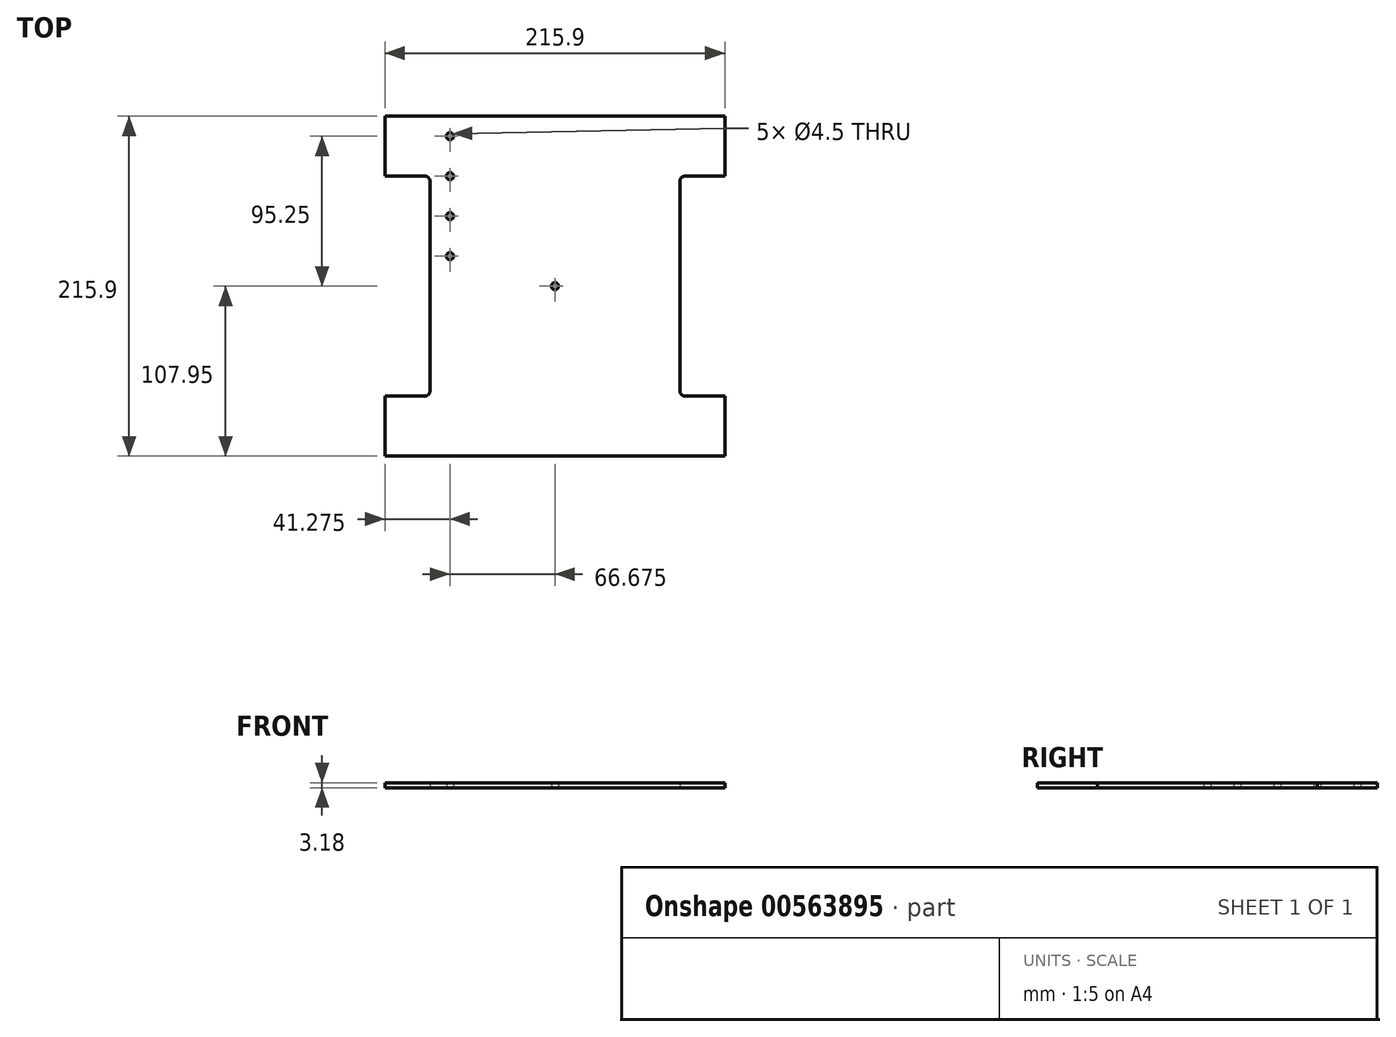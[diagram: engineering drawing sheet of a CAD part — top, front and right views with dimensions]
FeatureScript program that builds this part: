
annotation { "Feature Type Name" : "Feature", "Feature Type Description" : "" }
export const myFeature = defineFeature(function(context is Context, id is Id, definition is map)
    precondition{}
    {
        {
            var Q0;
            Q0=qCreatedBy(makeId("Top.planeOp"),FACE);
            var sketch = newSketch(context, id + "F0", { "sketchPlane" : qUnion([Q0])});
            skLineSegment(sketch, "E0", {"start": v(-107.95, -107.95) * mm, "end": v(107.95, -107.95) * mm});
            skLineSegment(sketch, "E1", {"start": v(107.95, -107.95) * mm, "end": v(107.95, -69.85) * mm});
            skLineSegment(sketch, "E2", {"start": v(107.95, -69.85) * mm, "end": v(82.55, -69.85) * mm});
            skLineSegment(sketch, "E3", {"start": v(79.37, -66.67) * mm, "end": v(79.37, 66.68) * mm});
            skLineSegment(sketch, "E4", {"start": v(82.55, 69.85) * mm, "end": v(107.95, 69.85) * mm});
            skLineSegment(sketch, "E5", {"start": v(107.95, 69.85) * mm, "end": v(107.95, 107.95) * mm});
            skLineSegment(sketch, "E6", {"start": v(107.95, 107.95) * mm, "end": v(-107.95, 107.95) * mm});
            skLineSegment(sketch, "E7", {"start": v(-107.95, 107.95) * mm, "end": v(-107.95, 69.85) * mm});
            skLineSegment(sketch, "E8", {"start": v(-107.95, 69.85) * mm, "end": v(-82.55, 69.85) * mm});
            skLineSegment(sketch, "E9", {"start": v(-79.38, 66.68) * mm, "end": v(-79.37, -66.68) * mm});
            skLineSegment(sketch, "E10", {"start": v(-82.55, -69.85) * mm, "end": v(-107.95, -69.85) * mm});
            skLineSegment(sketch, "E11", {"start": v(-107.95, -69.85) * mm, "end": v(-107.95, -107.95) * mm});
            skPoint(sketch, "E12.visualSharp", {"position": v(-79.38, 69.85) * mm});
            skArc(sketch, "E12.filletArc", {"start": v(-79.38, 66.68) * mm, "mid": v(-80.3, 68.92) * mm, "end": v(-82.55, 69.85) * mm});
            skPoint(sketch, "E13.visualSharp", {"position": v(79.37, 69.85) * mm});
            skArc(sketch, "E13.filletArc", {"start": v(82.55, 69.85) * mm, "mid": v(80.3, 68.92) * mm, "end": v(79.37, 66.68) * mm});
            skPoint(sketch, "E14.visualSharp", {"position": v(-79.37, -69.85) * mm});
            skArc(sketch, "E14.filletArc", {"start": v(-82.55, -69.85) * mm, "mid": v(-80.3, -68.92) * mm, "end": v(-79.37, -66.68) * mm});
            skPoint(sketch, "E15.visualSharp", {"position": v(79.37, -69.85) * mm});
            skArc(sketch, "E15.filletArc", {"start": v(79.37, -66.67) * mm, "mid": v(80.3, -68.92) * mm, "end": v(82.55, -69.85) * mm});
            skPoint(sketch, "E16", {"position": v(0, 0) * mm});
            skPoint(sketch, "E17", {"position": v(-69.85, 0) * mm});
            skPoint(sketch, "E18", {"position": v(-66.68, 95.25) * mm});
            skPoint(sketch, "E19", {"position": v(-66.68, 69.85) * mm});
            skPoint(sketch, "E20", {"position": v(-66.68, 44.45) * mm});
            skPoint(sketch, "E21", {"position": v(-66.68, 19.05) * mm});
            skPoint(sketch, "E22", {"position": v(65.86, 104.4) * mm});
            skPoint(sketch, "E23", {"position": v(65.86, 87.5) * mm});
            skPoint(sketch, "E24", {"position": v(65.86, 60.93) * mm});
            skPoint(sketch, "E25", {"position": v(65.86, 36.3) * mm});
            skPoint(sketch, "E26", {"position": v(65.86, 0) * mm});
            skPoint(sketch, "E27", {"position": v(65.86, -19.25) * mm});
            skPoint(sketch, "E28", {"position": v(65.86, -38.1) * mm});
            skPoint(sketch, "E29", {"position": v(65.86, -50.65) * mm});
            skPoint(sketch, "E30", {"position": v(65.86, -67.08) * mm});
            skPoint(sketch, "E31", {"position": v(-56.83, -14.9) * mm});
            skPoint(sketch, "E32", {"position": v(-56.83, -24.57) * mm});
            skPoint(sketch, "E33", {"position": v(-57.31, -42.44) * mm});
            skPoint(sketch, "E34", {"position": v(-55.86, -59.35) * mm});
            skPoint(sketch, "E35", {"position": v(-30.74, 110.2) * mm});
            skPoint(sketch, "E36", {"position": v(33.02, 110.2) * mm});
            skPoint(sketch, "E37", {"position": v(33.02, 87.5) * mm});
            skPoint(sketch, "E38", {"position": v(-30.74, 87.5) * mm});
            skSolve(sketch);
        }
        {
            var Q0;
            Q0 = qSketchRegion(id + "F0", true);
            extrude(context, id + "F1", {"entities" : qUnion([Q0]), "depth" : 3.17 * mm, "offsetDistance" : 25.4 * mm});
        }
        {
            var Q0;
            Q0=sQuery(id+"F0.wireOp",VERTEX,"E16");
            var Q1;
            Q1=makeQuery(id+"F1.opExtrude","SWEPT_BODY",BODY,{"disambiguationData":[OSD([sQuery(id+"F0.wireOp",EDGE,"E0"),sQuery(id+"F0.wireOp",EDGE,"E1"),sQuery(id+"F0.wireOp",EDGE,"E2"),sQuery(id+"F0.wireOp",EDGE,"E3"),sQuery(id+"F0.wireOp",EDGE,"E4"),sQuery(id+"F0.wireOp",EDGE,"E5"),sQuery(id+"F0.wireOp",EDGE,"E6"),sQuery(id+"F0.wireOp",EDGE,"E7"),sQuery(id+"F0.wireOp",EDGE,"E8"),sQuery(id+"F0.wireOp",EDGE,"E9"),sQuery(id+"F0.wireOp",EDGE,"E10"),sQuery(id+"F0.wireOp",EDGE,"E11"),sQuery(id+"F0.wireOp",EDGE,"E12.filletArc"),sQuery(id+"F0.wireOp",EDGE,"E13.filletArc"),sQuery(id+"F0.wireOp",EDGE,"E14.filletArc"),sQuery(id+"F0.wireOp",EDGE,"E15.filletArc")])]});
            hole(context, id + "F2", {"style" : HoleStyle.SIMPLE, "endStyle" : HoleEndStyle.THROUGH, "oppositeDirection" : true, "standardTappedOrClearance" : lookupTablePath({ "standard" : "ANSI", "fit" : "Normal (ASME)", "size" : "#8", "type" : "Clearance" }), "standardBlindInLast" : lookupTablePath({ "fit" : "Free", "standard" : "ANSI", "size" : "#8", "type" : "Clearance" }), "holeDiameter" : 4.5 * mm, "isTappedThrough" : true, "tappedDepth" : 12.7 * mm, "tapClearance" : 3, "locations" : qUnion([Q0]), "scope" : qUnion([Q1])});
        }
        {
            var Q0;
            Q0=sQuery(id+"F0.wireOp",VERTEX,"E18");
            var Q1;
            Q1=makeQuery(id+"F1.opExtrude","SWEPT_BODY",BODY,{"disambiguationData":[OSD([sQuery(id+"F0.wireOp",EDGE,"E0"),sQuery(id+"F0.wireOp",EDGE,"E1"),sQuery(id+"F0.wireOp",EDGE,"E2"),sQuery(id+"F0.wireOp",EDGE,"E3"),sQuery(id+"F0.wireOp",EDGE,"E4"),sQuery(id+"F0.wireOp",EDGE,"E5"),sQuery(id+"F0.wireOp",EDGE,"E6"),sQuery(id+"F0.wireOp",EDGE,"E7"),sQuery(id+"F0.wireOp",EDGE,"E8"),sQuery(id+"F0.wireOp",EDGE,"E9"),sQuery(id+"F0.wireOp",EDGE,"E10"),sQuery(id+"F0.wireOp",EDGE,"E11"),sQuery(id+"F0.wireOp",EDGE,"E12.filletArc"),sQuery(id+"F0.wireOp",EDGE,"E13.filletArc"),sQuery(id+"F0.wireOp",EDGE,"E14.filletArc"),sQuery(id+"F0.wireOp",EDGE,"E15.filletArc")])]});
            hole(context, id + "F3", {"style" : HoleStyle.SIMPLE, "endStyle" : HoleEndStyle.THROUGH, "oppositeDirection" : true, "standardTappedOrClearance" : lookupTablePath({ "standard" : "ANSI", "fit" : "Normal (ASME)", "size" : "#8", "type" : "Clearance" }), "standardBlindInLast" : lookupTablePath({ "fit" : "Free", "standard" : "ANSI", "size" : "#8", "type" : "Clearance" }), "holeDiameter" : 4.5 * mm, "isTappedThrough" : true, "tappedDepth" : 12.7 * mm, "tapClearance" : 3, "locations" : qUnion([Q0]), "scope" : qUnion([Q1])});
        }
        {
            var Q0;
            Q0=sQuery(id+"F0.wireOp",VERTEX,"E19");
            var Q1;
            Q1=makeQuery(id+"F1.opExtrude","SWEPT_BODY",BODY,{"disambiguationData":[OSD([sQuery(id+"F0.wireOp",EDGE,"E0"),sQuery(id+"F0.wireOp",EDGE,"E1"),sQuery(id+"F0.wireOp",EDGE,"E2"),sQuery(id+"F0.wireOp",EDGE,"E3"),sQuery(id+"F0.wireOp",EDGE,"E4"),sQuery(id+"F0.wireOp",EDGE,"E5"),sQuery(id+"F0.wireOp",EDGE,"E6"),sQuery(id+"F0.wireOp",EDGE,"E7"),sQuery(id+"F0.wireOp",EDGE,"E8"),sQuery(id+"F0.wireOp",EDGE,"E9"),sQuery(id+"F0.wireOp",EDGE,"E10"),sQuery(id+"F0.wireOp",EDGE,"E11"),sQuery(id+"F0.wireOp",EDGE,"E12.filletArc"),sQuery(id+"F0.wireOp",EDGE,"E13.filletArc"),sQuery(id+"F0.wireOp",EDGE,"E14.filletArc"),sQuery(id+"F0.wireOp",EDGE,"E15.filletArc")])]});
            hole(context, id + "F4", {"style" : HoleStyle.SIMPLE, "endStyle" : HoleEndStyle.THROUGH, "oppositeDirection" : true, "standardTappedOrClearance" : lookupTablePath({ "standard" : "ANSI", "fit" : "Normal (ASME)", "size" : "#8", "type" : "Clearance" }), "standardBlindInLast" : lookupTablePath({ "fit" : "Free", "standard" : "ANSI", "size" : "#8", "type" : "Clearance" }), "holeDiameter" : 4.5 * mm, "isTappedThrough" : true, "tappedDepth" : 12.7 * mm, "tapClearance" : 3, "locations" : qUnion([Q0]), "scope" : qUnion([Q1])});
        }
        {
            var Q0;
            Q0=sQuery(id+"F0.wireOp",VERTEX,"E20");
            var Q1;
            Q1=makeQuery(id+"F1.opExtrude","SWEPT_BODY",BODY,{"disambiguationData":[OSD([sQuery(id+"F0.wireOp",EDGE,"E0"),sQuery(id+"F0.wireOp",EDGE,"E1"),sQuery(id+"F0.wireOp",EDGE,"E2"),sQuery(id+"F0.wireOp",EDGE,"E3"),sQuery(id+"F0.wireOp",EDGE,"E4"),sQuery(id+"F0.wireOp",EDGE,"E5"),sQuery(id+"F0.wireOp",EDGE,"E6"),sQuery(id+"F0.wireOp",EDGE,"E7"),sQuery(id+"F0.wireOp",EDGE,"E8"),sQuery(id+"F0.wireOp",EDGE,"E9"),sQuery(id+"F0.wireOp",EDGE,"E10"),sQuery(id+"F0.wireOp",EDGE,"E11"),sQuery(id+"F0.wireOp",EDGE,"E12.filletArc"),sQuery(id+"F0.wireOp",EDGE,"E13.filletArc"),sQuery(id+"F0.wireOp",EDGE,"E14.filletArc"),sQuery(id+"F0.wireOp",EDGE,"E15.filletArc")])]});
            hole(context, id + "F5", {"style" : HoleStyle.SIMPLE, "endStyle" : HoleEndStyle.THROUGH, "oppositeDirection" : true, "standardTappedOrClearance" : lookupTablePath({ "standard" : "ANSI", "fit" : "Normal (ASME)", "size" : "#8", "type" : "Clearance" }), "standardBlindInLast" : lookupTablePath({ "fit" : "Free", "standard" : "ANSI", "size" : "#8", "type" : "Clearance" }), "holeDiameter" : 4.5 * mm, "isTappedThrough" : true, "tappedDepth" : 12.7 * mm, "tapClearance" : 3, "locations" : qUnion([Q0]), "scope" : qUnion([Q1])});
        }
        {
            var Q0;
            Q0=sQuery(id+"F0.wireOp",VERTEX,"E21");
            var Q1;
            Q1=makeQuery(id+"F1.opExtrude","SWEPT_BODY",BODY,{"disambiguationData":[OSD([sQuery(id+"F0.wireOp",EDGE,"E0"),sQuery(id+"F0.wireOp",EDGE,"E1"),sQuery(id+"F0.wireOp",EDGE,"E2"),sQuery(id+"F0.wireOp",EDGE,"E3"),sQuery(id+"F0.wireOp",EDGE,"E4"),sQuery(id+"F0.wireOp",EDGE,"E5"),sQuery(id+"F0.wireOp",EDGE,"E6"),sQuery(id+"F0.wireOp",EDGE,"E7"),sQuery(id+"F0.wireOp",EDGE,"E8"),sQuery(id+"F0.wireOp",EDGE,"E9"),sQuery(id+"F0.wireOp",EDGE,"E10"),sQuery(id+"F0.wireOp",EDGE,"E11"),sQuery(id+"F0.wireOp",EDGE,"E12.filletArc"),sQuery(id+"F0.wireOp",EDGE,"E13.filletArc"),sQuery(id+"F0.wireOp",EDGE,"E14.filletArc"),sQuery(id+"F0.wireOp",EDGE,"E15.filletArc")])]});
            hole(context, id + "F6", {"style" : HoleStyle.SIMPLE, "endStyle" : HoleEndStyle.THROUGH, "oppositeDirection" : true, "standardTappedOrClearance" : lookupTablePath({ "standard" : "ANSI", "fit" : "Normal (ASME)", "size" : "#8", "type" : "Clearance" }), "standardBlindInLast" : lookupTablePath({ "fit" : "Free", "standard" : "ANSI", "size" : "#8", "type" : "Clearance" }), "holeDiameter" : 4.5 * mm, "isTappedThrough" : true, "tappedDepth" : 12.7 * mm, "tapClearance" : 3, "locations" : qUnion([Q0]), "scope" : qUnion([Q1])});
        }
    });
